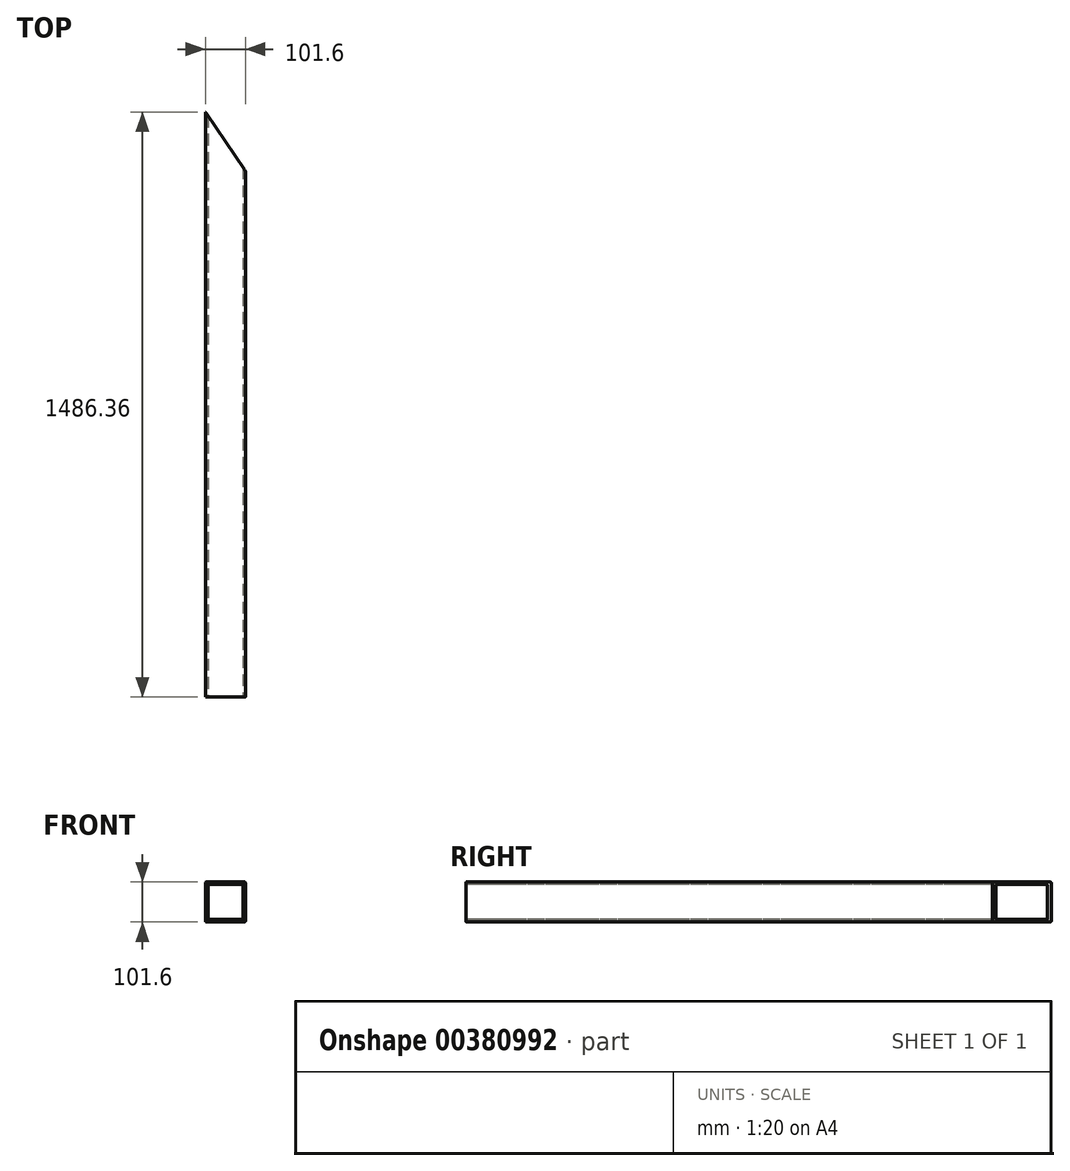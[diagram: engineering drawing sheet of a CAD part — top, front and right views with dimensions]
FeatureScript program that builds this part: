
annotation { "Feature Type Name" : "Feature", "Feature Type Description" : "" }
export const myFeature = defineFeature(function(context is Context, id is Id, definition is map)
    precondition{}
    {
        {
            var Q0;
            Q0=qCreatedBy(makeId("Top.planeOp"),FACE);
            var sketch = newSketch(context, id + "F0", { "sketchPlane" : qUnion([Q0])});
            skLineSegment(sketch, "E0.right", {"start": v(-560, 75) * mm, "end": v(-560, -75) * mm});
            skLineSegment(sketch, "E1.top", {"start": v(-560, -1035) * mm, "end": v(-458.4, -1035) * mm});
            skLineSegment(sketch, "E1.left", {"start": v(-560, 75) * mm, "end": v(-560, -1035) * mm});
            skLineSegment(sketch, "E1.right", {"start": v(-458.4, -75) * mm, "end": v(-458.4, -1035) * mm});
            skLineSegment(sketch, "E2", {"start": v(-458.4, -75) * mm, "end": v(-560, 75) * mm});
            skLineSegment(sketch, "E3.right", {"start": v(-560, 451.36) * mm, "end": v(-560, 301.36) * mm});
            skPoint(sketch, "E3.middle", {"position": v(0, 376.36) * mm});
            skLineSegment(sketch, "E4.top", {"start": v(-560, -658.64) * mm, "end": v(-458.4, -658.64) * mm});
            skLineSegment(sketch, "E4.left", {"start": v(-560, 451.36) * mm, "end": v(-560, -658.64) * mm});
            skLineSegment(sketch, "E4.right", {"start": v(-458.4, 301.36) * mm, "end": v(-458.4, -658.64) * mm});
            skLineSegment(sketch, "E5", {"start": v(-458.4, 301.36) * mm, "end": v(-560, 451.36) * mm});
            skSolve(sketch);
        }
        {
            var Q0;
            Q0 = qSketchRegion(id + "F0", true);
            extrude(context, id + "F1", {"entities" : qUnion([Q0]), "endBound" : BoundingType.SYMMETRIC, "depth" : 101.6 * mm});
        }
        {
            var Q0;
            Q0=makeQuery(id+"F1.opExtrude","SWEPT_FACE",FACE,{"disambiguationData":[OSD([sQuery(id+"F0.wireOp",EDGE,"E1.top")])]});
            var sketch = newSketch(context, id + "F2", { "sketchPlane" : qUnion([Q0])});
            skLineSegment(sketch, "E6.bottom", {"start": v(-464.75, 44.45) * mm, "end": v(-553.65, 44.45) * mm});
            skLineSegment(sketch, "E6.top", {"start": v(-464.75, -44.45) * mm, "end": v(-553.65, -44.45) * mm});
            skLineSegment(sketch, "E6.left", {"start": v(-464.75, 44.45) * mm, "end": v(-464.75, -44.45) * mm});
            skLineSegment(sketch, "E6.right", {"start": v(-553.65, 44.45) * mm, "end": v(-553.65, -44.45) * mm});
            skPoint(sketch, "E6.middle", {"position": v(-509.2, 0) * mm});
            skPoint(sketch, "E6.middle.positionSnap0", {"position": v(-509.2, 50.8) * mm});
            skPoint(sketch, "E6.middle.positionSnap1", {"position": v(-458.4, 0) * mm});
            skPoint(sketch, "E6.centerSnap0", {"position": v(-509.2, 50.8) * mm});
            skPoint(sketch, "E6.centerSnap1", {"position": v(-458.4, 0) * mm});
            skSolve(sketch);
        }
        {
            var Q0;
            Q0=makeQuery(id+"F2.imprint","IMPRINT",FACE,{"disambiguationData":[TD([[makeQuery(id+"F2.imprint","IMPRINT",EDGE,{"derivedFrom":sQuery(id+"F2.wireOp",EDGE,"E6.bottom")}),1.0]])]});
            extrude(context, id + "F3", {"entities" : qUnion([Q0]), "operationType" : NewBodyOperationType.REMOVE, "endBound" : BoundingType.UP_TO_NEXT, "oppositeDirection" : true, "depth" : 25 * mm});
        }
        {
            var Q0;
            Q0=makeQuery(id+"F3.boolean.opBoolean","COPY",EDGE,{"derivedFrom":makeQuery(id+"F3.opExtrude","SWEPT_EDGE",EDGE,{"disambiguationData":[OSD([sQuery(id+"F2.wireOp",EDGE,"E6.top"),sQuery(id+"F2.wireOp",EDGE,"E6.right")])]})});
            var Q1;
            Q1=makeQuery(id+"F3.boolean.opBoolean","COPY",EDGE,{"derivedFrom":makeQuery(id+"F3.opExtrude","SWEPT_EDGE",EDGE,{"disambiguationData":[OSD([sQuery(id+"F2.wireOp",EDGE,"E6.top"),sQuery(id+"F2.wireOp",EDGE,"E6.left")])]})});
            var Q2;
            Q2=makeQuery(id+"F3.boolean.opBoolean","COPY",EDGE,{"derivedFrom":makeQuery(id+"F3.opExtrude","SWEPT_EDGE",EDGE,{"disambiguationData":[OSD([sQuery(id+"F2.wireOp",EDGE,"E6.bottom"),sQuery(id+"F2.wireOp",EDGE,"E6.left")])]})});
            var Q3;
            Q3=makeQuery(id+"F3.boolean.opBoolean","COPY",EDGE,{"derivedFrom":makeQuery(id+"F3.opExtrude","SWEPT_EDGE",EDGE,{"disambiguationData":[OSD([sQuery(id+"F2.wireOp",EDGE,"E6.bottom"),sQuery(id+"F2.wireOp",EDGE,"E6.right")])]})});
            var Q4;
            Q4=makeQuery(id+"F1.opExtrude","CAP_EDGE",EDGE,{"disambiguationData":[OSD([sQuery(id+"F0.wireOp",EDGE,"E1.right"),sQuery(id+"F0.wireOp",EDGE,"E4.right")])],"isStart":false});
            var Q5;
            Q5=makeQuery(id+"F1.opExtrude","CAP_EDGE",EDGE,{"disambiguationData":[OSD([sQuery(id+"F0.wireOp",EDGE,"E1.right"),sQuery(id+"F0.wireOp",EDGE,"E4.right")])],"isStart":true});
            var Q6;
            Q6=makeQuery(id+"F1.opExtrude","CAP_EDGE",EDGE,{"disambiguationData":[OSD([sQuery(id+"F0.wireOp",EDGE,"E1.left"),sQuery(id+"F0.wireOp",EDGE,"E4.left")])],"isStart":true});
            var Q7;
            Q7=makeQuery(id+"F1.opExtrude","CAP_EDGE",EDGE,{"disambiguationData":[OSD([sQuery(id+"F0.wireOp",EDGE,"E1.left"),sQuery(id+"F0.wireOp",EDGE,"E4.left")])],"isStart":false});
            fillet(context, id + "F4", {"entities" : qUnion([Q0, Q1, Q2, Q3, Q4, Q5, Q6, Q7]), "radius" : 2.5 * mm, "tangentPropagation" : true, "allowEdgeOverflow" : false});
        }
    });
